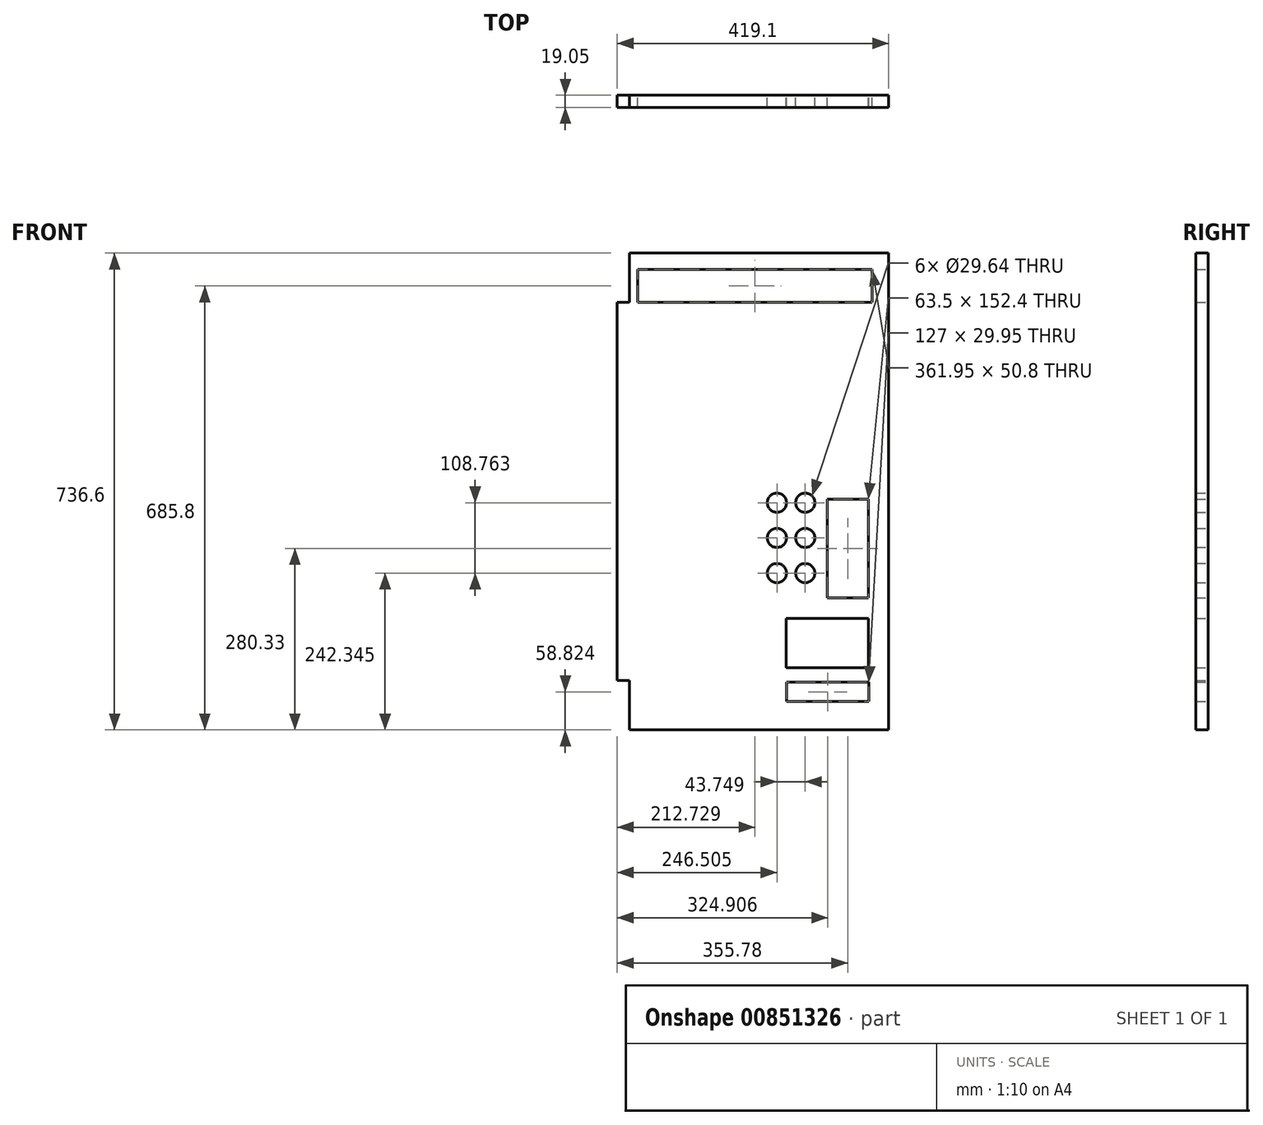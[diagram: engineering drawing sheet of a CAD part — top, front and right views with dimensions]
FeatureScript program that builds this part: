
annotation { "Feature Type Name" : "Feature", "Feature Type Description" : "" }
export const myFeature = defineFeature(function(context is Context, id is Id, definition is map)
    precondition{}
    {
        {
            var Q0;
            Q0=qCreatedBy(makeId("Front.planeOp"),FACE);
            var sketch = newSketch(context, id + "F0", { "sketchPlane" : qUnion([Q0])});
            skLineSegment(sketch, "E0", {"start": v(202.55, -510.7) * mm, "end": v(202.55, 225.9) * mm});
            skLineSegment(sketch, "E1", {"start": v(170.98, -154.17) * mm, "end": v(107.48, -154.17) * mm});
            skLineSegment(sketch, "E2", {"start": v(107.48, -154.17) * mm, "end": v(107.48, -306.57) * mm});
            skLineSegment(sketch, "E3", {"start": v(107.48, -306.57) * mm, "end": v(170.98, -306.57) * mm});
            skLineSegment(sketch, "E4", {"start": v(170.98, -306.57) * mm, "end": v(170.98, -154.17) * mm});
            skLineSegment(sketch, "E5", {"start": v(170.98, -338.63) * mm, "end": v(43.98, -338.63) * mm});
            skLineSegment(sketch, "E6", {"start": v(43.98, -338.63) * mm, "end": v(43.98, -414.83) * mm});
            skLineSegment(sketch, "E7", {"start": v(43.98, -414.83) * mm, "end": v(170.98, -414.83) * mm});
            skLineSegment(sketch, "E8", {"start": v(170.98, -414.83) * mm, "end": v(170.98, -338.63) * mm});
            skLineSegment(sketch, "E9", {"start": v(44.86, -436.9) * mm, "end": v(44.86, -466.85) * mm});
            skLineSegment(sketch, "E10", {"start": v(44.86, -466.85) * mm, "end": v(171.86, -466.85) * mm});
            skLineSegment(sketch, "E11", {"start": v(171.86, -466.85) * mm, "end": v(171.86, -436.9) * mm});
            skLineSegment(sketch, "E12", {"start": v(171.86, -436.9) * mm, "end": v(44.86, -436.9) * mm});
            skCircle(sketch, "E13", {"center": v(73.7, -159.6) * mm, "radius": 14.82 * mm});
            skCircle(sketch, "E14", {"center": v(29.96, -159.6) * mm, "radius": 14.82 * mm});
            skCircle(sketch, "E15", {"center": v(29.95, -213.96) * mm, "radius": 14.82 * mm});
            skCircle(sketch, "E16", {"center": v(73.7, -213.97) * mm, "radius": 14.82 * mm});
            skCircle(sketch, "E17", {"center": v(73.7, -268.36) * mm, "radius": 14.82 * mm});
            skCircle(sketch, "E18", {"center": v(29.95, -268.36) * mm, "radius": 14.82 * mm});
            skLineSegment(sketch, "E19.bottom", {"start": v(-184.8, 200.5) * mm, "end": v(177.15, 200.5) * mm});
            skLineSegment(sketch, "E19.top", {"start": v(-184.8, 149.7) * mm, "end": v(177.15, 149.7) * mm});
            skLineSegment(sketch, "E19.left", {"start": v(-184.8, 200.5) * mm, "end": v(-184.8, 149.7) * mm});
            skLineSegment(sketch, "E19.right", {"start": v(177.15, 200.5) * mm, "end": v(177.15, 149.7) * mm});
            skLineSegment(sketch, "E20", {"start": v(-197.5, -510.7) * mm, "end": v(-197.5, -434.5) * mm});
            skLineSegment(sketch, "E21", {"start": v(-197.5, -434.5) * mm, "end": v(-216.55, -434.5) * mm});
            skLineSegment(sketch, "E22.top", {"start": v(-216.55, 149.7) * mm, "end": v(-197.5, 149.7) * mm});
            skLineSegment(sketch, "E22.right", {"start": v(-197.5, 225.9) * mm, "end": v(-197.5, 149.7) * mm});
            skLineSegment(sketch, "E23", {"start": v(-216.55, 149.7) * mm, "end": v(-216.55, -434.5) * mm});
            skLineSegment(sketch, "E24", {"start": v(-197.5, 225.9) * mm, "end": v(202.55, 225.9) * mm});
            skLineSegment(sketch, "E25", {"start": v(-197.5, -510.7) * mm, "end": v(202.55, -510.7) * mm});
            skSolve(sketch);
        }
        {
            var Q0;
            Q0=makeQuery(id+"F0.imprint","IMPRINT",FACE,{"disambiguationData":[TD([[makeQuery(id+"F0.imprint","IMPRINT",EDGE,{"derivedFrom":sQuery(id+"F0.wireOp",EDGE,"E0")}),1.0]])]});
            extrude(context, id + "F1", {"entities" : qUnion([Q0]), "depth" : 19.05 * mm, "offsetDistance" : 25.4 * mm});
        }
    });
